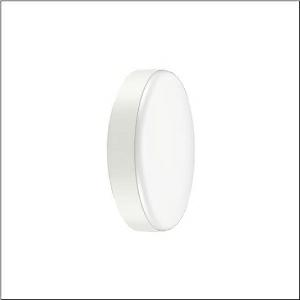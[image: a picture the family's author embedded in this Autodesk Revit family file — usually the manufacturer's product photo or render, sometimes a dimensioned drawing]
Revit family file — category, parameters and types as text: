
# Revit family: rondel_31_51wc10mb34a
name_source: partatom
category: Lighting Fixtures
units: mm (PartAtom-declared; Revit-internal decimal feet)

## family parameters
Cut with Voids When Loaded = No
Host = Face
Light Source = No
Part Type = Normal
Room Calculation Point = No
Round Connector Dimension = Use Diameter
Shared = No

## types (1)
- --- (1 x LED, 4250 lm, 34 W, 3000K)
    Apparent Load = 34 VA
    CIE Flux Codes = 44 75 94 94 100
    Color Rendering = 80
    Color Temperature = 3000K
    Default Elevation = 1800 mm
    Description = Rondel 31, wall and ceiling luminaire, primary optical cover: cover, of PC, opal, light emission: direct distribution, primary light characteristic: symmetric, installation type: surface-mounted, LED, rated luminous flux: 4.100lm, luminous efficacy: 120lm/W, light colour: 830, colour temperature: 3000K, with terminal, 3-pole, max. 2.5mm², mains connection: 220..240V, AC, 50/60Hz, rated input power: 34W, luminaire housing, of PC, traffic white (RAL 9016), diameter: 480mm, protection rating (complete): IP65, insulation class (complete): insulation class II (safety insulation), certification: CE, impact resistance: IK10, permissible storage temperature: -20..+60°C, packaging unit: 1 piece
    Height = 97 mm
    Lamp = 1 x LED
    Lamp Light Flux = 4250 lm
    Lamp Power = 34 W
    Lamp count = 1
    Length = 480 mm
    Luminous efficacy = 125 lm/W
    Manufacturer = Siteco
    ModVariant = No
    Model = 51WC10MB34A
    Mounting Place = Ceiling
    Mounting Type = Surface mounted
    Number of Poles = 1
    OnlyDefault = Yes
    Power Factor = 1
    Product Name = Rondel 31
    Product group = wall and ceiling luminaire
    ProductGroupID = 301
    Protection Class = Protection class II
    Protection Degree = IP 65
    RLX_Detail_Level = 1
    RlxData = <blob elided: 41337 chars, md5=84b964c1>
    Socket = socket
    Standby Power = 0 W
    System Light Flux = 4250 lm
    System Power = 34 W
    Type Comments = factory setting: luminous flux: 100 % | (ON | ON)
    Type Image = l_1007188.jpg
    URL = http://relux.com
    VarID = @adj_060581
    Voltage = 0 V
    Weight = 0.00 kg
    Width = 0 mm  [stored 0 ft]

note: [stored X ft] marks values corroborated as IEEE doubles in the binary element streams (Revit-internal decimal feet)

## geometry (parser evidence)
native form markers: Blend x4, Sweep x13
no freeform markers — native parametric forms only
